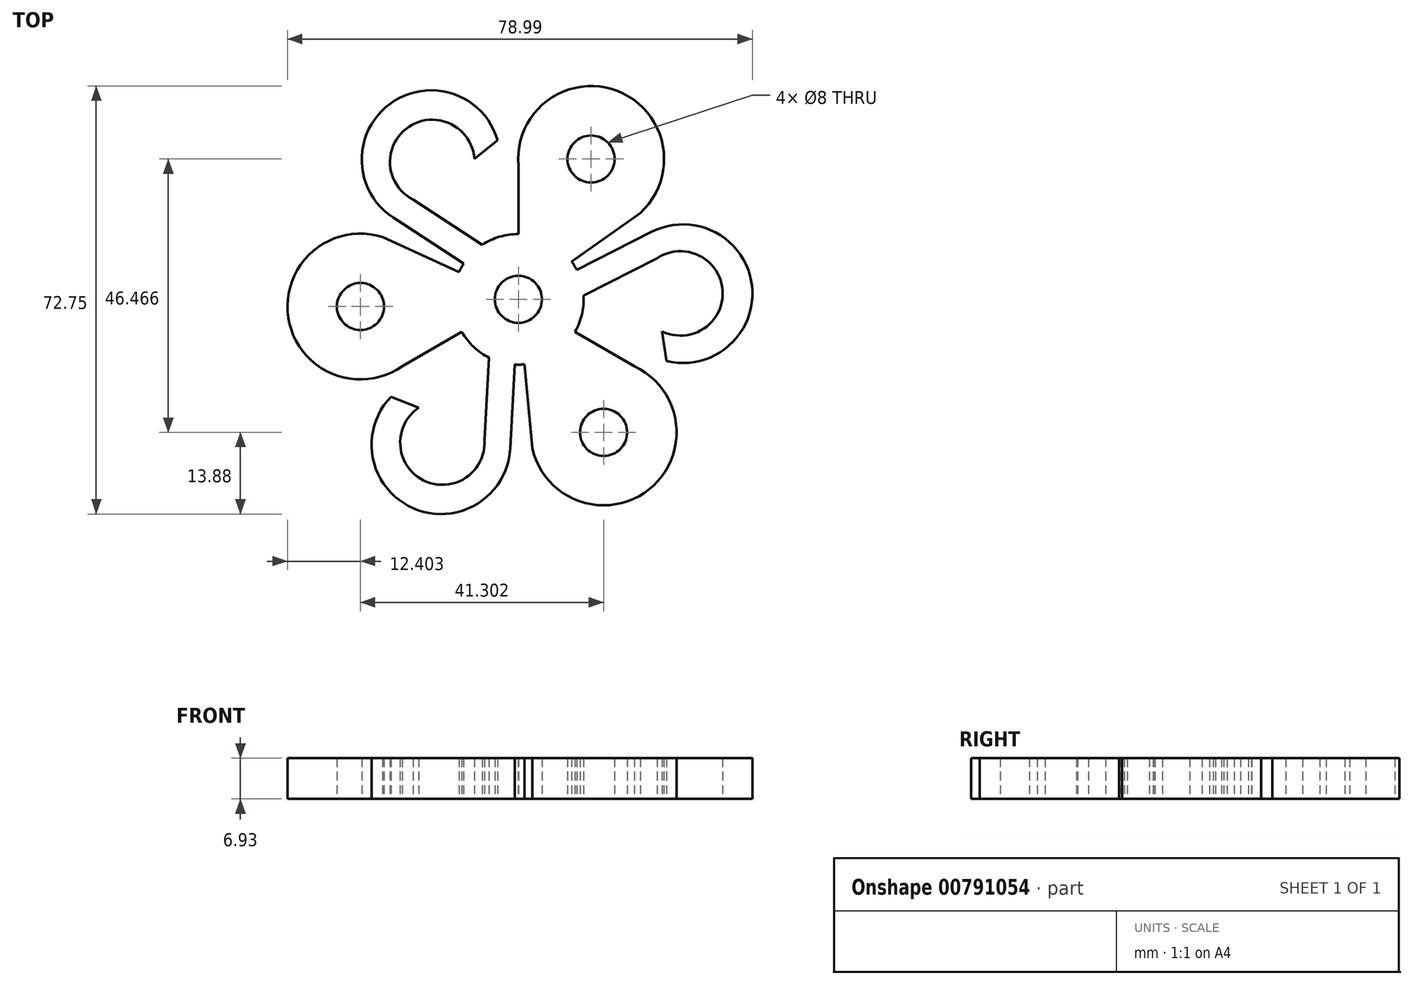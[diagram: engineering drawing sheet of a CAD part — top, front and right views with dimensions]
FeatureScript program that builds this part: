
annotation { "Feature Type Name" : "Feature", "Feature Type Description" : "" }
export const myFeature = defineFeature(function(context is Context, id is Id, definition is map)
    precondition{}
    {
        {
            var Q0;
            Q0=qCreatedBy(makeId("Top.planeOp"),FACE);
            var sketch = newSketch(context, id + "F0", { "sketchPlane" : qUnion([Q0])});
            skLineSegment(sketch, "E0", {"start": v(0, 0) * mm, "end": v(3.26, 2.31) * mm});
            skLineSegment(sketch, "E1", {"start": v(0, 0) * mm, "end": v(-3.35, 2.19) * mm});
            skArc(sketch, "E2", {"start": v(20.72, 14.7) * mm, "mid": v(16.85, 35.4) * mm, "end": v(0, 22.75) * mm});
            skArc(sketch, "E3", {"start": v(-3.51, 27.03) * mm, "mid": v(-21.84, 33.22) * mm, "end": v(-21.27, 13.89) * mm});
            skLineSegment(sketch, "E4", {"start": v(-3.51, 27.03) * mm, "end": v(-7.48, 23.85) * mm});
            skArc(sketch, "E5", {"start": v(-7.48, 23.85) * mm, "mid": v(-18.61, 29.33) * mm, "end": v(-17.86, 16.95) * mm});
            skLineSegment(sketch, "E6", {"start": v(-17.86, 16.95) * mm, "end": v(-6.1, 9.27) * mm});
            skLineSegment(sketch, "E7", {"start": v(0, 5.28) * mm, "end": v(0, 22.75) * mm});
            skCircle(sketch, "E8", {"center": v(12.35, 23.85) * mm, "radius": 4 * mm});
            skCircle(sketch, "E9", {"center": v(0, 0) * mm, "radius": 4 * mm});
            skCircle(sketch, "E10", {"center": v(0, 0) * mm, "radius": 11.1 * mm});
            skLineSegment(sketch, "E11.1.0", {"start": v(-5.75, -23.95) * mm, "end": v(-4.98, -9.92) * mm});
            skArc(sketch, "E11.1.1", {"start": v(-23.08, 10.6) * mm, "mid": v(-39.08, -3.11) * mm, "end": v(-19.7, -11.38) * mm});
            skLineSegment(sketch, "E11.1.2", {"start": v(0, 0) * mm, "end": v(-3.64, 1.67) * mm});
            skLineSegment(sketch, "E11.1.3", {"start": v(-9.61, -5.55) * mm, "end": v(-19.7, -11.38) * mm});
            skLineSegment(sketch, "E11.1.4", {"start": v(0, 0) * mm, "end": v(-0.22, -4) * mm});
            skArc(sketch, "E11.1.5", {"start": v(-21.65, -16.55) * mm, "mid": v(-17.85, -35.52) * mm, "end": v(-1.4, -25.36) * mm});
            skArc(sketch, "E11.1.6", {"start": v(-16.9, -18.4) * mm, "mid": v(-16.1, -30.78) * mm, "end": v(-5.75, -23.95) * mm});
            skLineSegment(sketch, "E11.1.7", {"start": v(-21.65, -16.55) * mm, "end": v(-16.9, -18.4) * mm});
            skCircle(sketch, "E11.1.8", {"center": v(-26.83, -1.22) * mm, "radius": 4 * mm});
            skLineSegment(sketch, "E11.2.0", {"start": v(23.61, 7) * mm, "end": v(11.08, 0.65) * mm});
            skArc(sketch, "E11.2.1", {"start": v(2.36, -25.29) * mm, "mid": v(22.24, -32.3) * mm, "end": v(19.7, -11.38) * mm});
            skLineSegment(sketch, "E11.2.2", {"start": v(0, 0) * mm, "end": v(0.37, -3.98) * mm});
            skLineSegment(sketch, "E11.2.3", {"start": v(9.61, -5.55) * mm, "end": v(19.7, -11.38) * mm});
            skLineSegment(sketch, "E11.2.4", {"start": v(0, 0) * mm, "end": v(3.57, 1.8) * mm});
            skArc(sketch, "E11.2.5", {"start": v(25.16, -10.47) * mm, "mid": v(39.69, 2.3) * mm, "end": v(22.66, 11.48) * mm});
            skArc(sketch, "E11.2.6", {"start": v(24.4, -5.44) * mm, "mid": v(34.7, 1.45) * mm, "end": v(23.61, 7) * mm});
            skLineSegment(sketch, "E11.2.7", {"start": v(25.16, -10.47) * mm, "end": v(24.4, -5.44) * mm});
            skCircle(sketch, "E11.2.8", {"center": v(14.47, -22.62) * mm, "radius": 4 * mm});
            skPoint(sketch, "E12.orphan", {"position": v(-4.58, -2.64) * mm});
            skLineSegment(sketch, "E13.trimOffspring", {"start": v(-10.09, 4.63) * mm, "end": v(-23.08, 10.6) * mm});
            skLineSegment(sketch, "E14.trimOffspring", {"start": v(-9.3, 6.07) * mm, "end": v(-21.27, 13.89) * mm});
            skLineSegment(sketch, "E15.trimOffspring", {"start": v(1.03, -11.05) * mm, "end": v(2.36, -25.29) * mm});
            skLineSegment(sketch, "E16.trimOffspring", {"start": v(-0.6, -11.08) * mm, "end": v(-1.4, -25.36) * mm});
            skPoint(sketch, "E17.orphan", {"position": v(4.58, -2.64) * mm});
            skLineSegment(sketch, "E18.trimOffspring", {"start": v(9.05, 6.42) * mm, "end": v(20.72, 14.7) * mm});
            skLineSegment(sketch, "E19.trimOffspring", {"start": v(9.9, 5.01) * mm, "end": v(22.66, 11.48) * mm});
            skSolve(sketch);
        }
        {
            var Q0;
            {var subQ4=sQuery(id+"F0.wireOp",EDGE,"E2");Q0=makeQuery(id+"F0.imprint","IMPRINT",FACE,{"disambiguationData":[TD([[makeQuery(id+"F0.imprint","IMPRINT",EDGE,{"derivedFrom":subQ4}),1.0]])]});}
            var Q1;
            Q1=makeQuery(id+"F0.imprint","IMPRINT",FACE,{"disambiguationData":[TD([[makeQuery(id+"F0.imprint","IMPRINT",EDGE,{"derivedFrom":sQuery(id+"F0.wireOp",EDGE,"E11.2.1")}),1.0]])]});
            var Q2;
            {var subQ0=sQuery(id+"F0.wireOp",EDGE,"E11.2.0");Q2=makeQuery(id+"F0.imprint","IMPRINT",FACE,{"disambiguationData":[TD([[makeQuery(id+"F0.imprint","IMPRINT",EDGE,{"derivedFrom":subQ0}),-1.0]])]});}
            var Q3;
            {var subQ0=sQuery(id+"F0.wireOp",EDGE,"E11.1.0");Q3=makeQuery(id+"F0.imprint","IMPRINT",FACE,{"disambiguationData":[TD([[makeQuery(id+"F0.imprint","IMPRINT",EDGE,{"derivedFrom":subQ0}),-1.0]])]});}
            var Q4;
            Q4=makeQuery(id+"F0.imprint","IMPRINT",FACE,{"disambiguationData":[TD([[makeQuery(id+"F0.imprint","IMPRINT",EDGE,{"derivedFrom":sQuery(id+"F0.wireOp",EDGE,"E11.1.1")}),1.0]])]});
            var Q5;
            Q5=makeQuery(id+"F0.imprint","IMPRINT",FACE,{"disambiguationData":[TD([[makeQuery(id+"F0.imprint","IMPRINT",EDGE,{"derivedFrom":sQuery(id+"F0.wireOp",EDGE,"E3")}),1.0]])]});
            var Q6;
            {var subQ6=sQuery(id+"F0.wireOp",EDGE,"E9");var subQ10=makeQuery(id+"F0.imprint","INTERSECT",VERTEX,{"derivedFrom":[sQuery(id+"F0.wireOp",EDGE,"E0"),subQ6]});Q6=makeQuery(id+"F0.imprint","IMPRINT",FACE,{"disambiguationData":[TD([[makeQuery(id+"F0.imprint","IMPRINT",EDGE,{"disambiguationData":[TD([[subQ10,1.0]])],"derivedFrom":subQ6}),-1.0]])]});}
            extrude(context, id + "F1", {"entities" : qUnion([Q0, Q1, Q2, Q3, Q4, Q5, Q6]), "depth" : 6.93 * mm, "offsetDistance" : 25.4 * mm});
        }
    });
